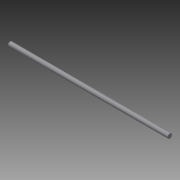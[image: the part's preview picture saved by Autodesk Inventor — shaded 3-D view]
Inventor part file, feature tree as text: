
AUTODESK INVENTOR PART (.ipt)
format: ipt  version: 2015 (Build 190159000, 159)  size: 70,144 bytes
history: native  units: in
note: dims shown in document units (in); Inventor stores cm internally (conversion verified against a paired STEP export)
features: extrude x1, sketch x1
ambient origin geometry x8: Origin, YZ Plane, XZ Plane, XY Plane, X Axis, Y Axis, Z Axis, Center Point
bodies: Solid1 (feature_tree)
feature tree (2):
  extrude  "Extrusion1"  Depth=8.875in TaperAngle=0.0deg
  sketch  "Sketch1"  dims[d0=0.25in d1=8.875in d2=0.0in]
